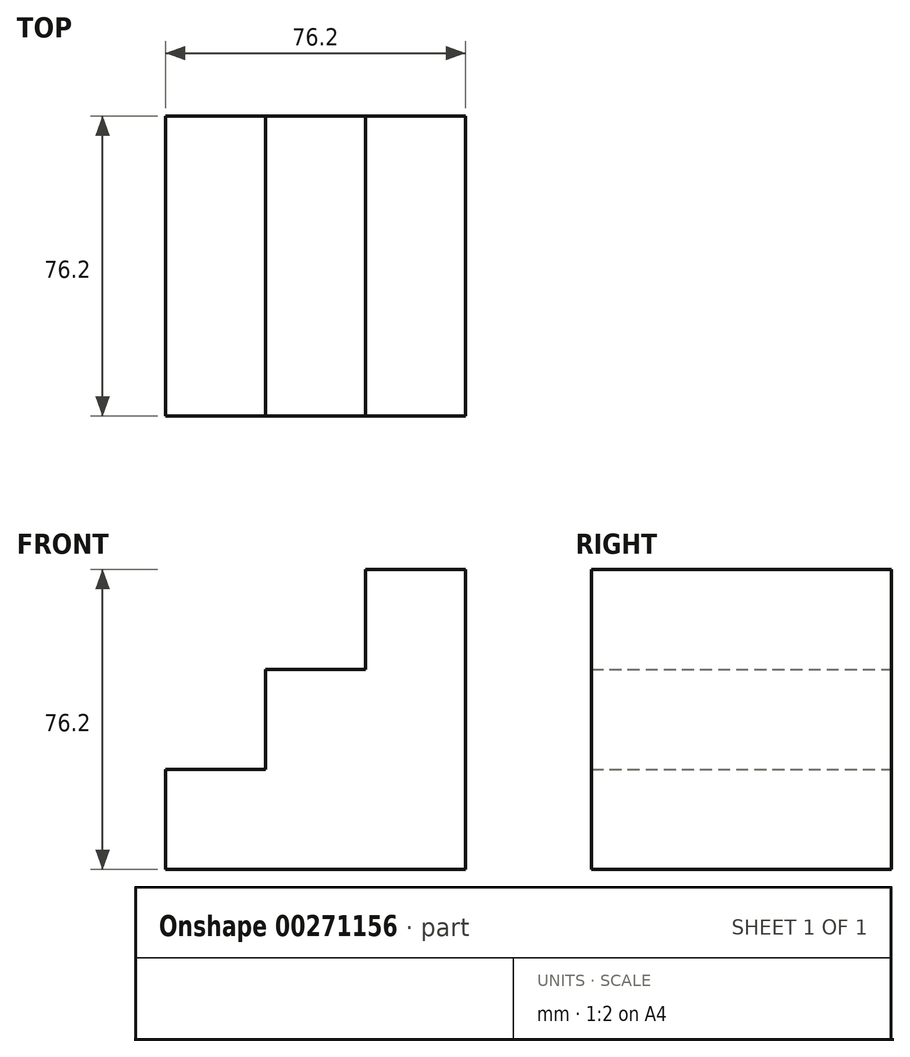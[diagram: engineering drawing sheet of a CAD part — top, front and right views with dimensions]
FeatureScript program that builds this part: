
annotation { "Feature Type Name" : "Feature", "Feature Type Description" : "" }
export const myFeature = defineFeature(function(context is Context, id is Id, definition is map)
    precondition{}
    {
        {
            var Q0;
            Q0=qCreatedBy(makeId("Front.planeOp"),FACE);
            var sketch = newSketch(context, id + "F0", { "sketchPlane" : qUnion([Q0])});
            skLineSegment(sketch, "E0", {"start": v(0, 0) * mm, "end": v(-76.2, 0) * mm});
            skLineSegment(sketch, "E1", {"start": v(-76.2, 0) * mm, "end": v(-76.2, 25.4) * mm});
            skLineSegment(sketch, "E2", {"start": v(-76.2, 25.4) * mm, "end": v(-50.8, 25.4) * mm});
            skLineSegment(sketch, "E3", {"start": v(-50.8, 25.4) * mm, "end": v(-50.8, 50.8) * mm});
            skLineSegment(sketch, "E4", {"start": v(-50.8, 50.8) * mm, "end": v(-25.4, 50.8) * mm});
            skLineSegment(sketch, "E5", {"start": v(-25.4, 50.8) * mm, "end": v(-25.4, 76.2) * mm});
            skLineSegment(sketch, "E6", {"start": v(-25.4, 76.2) * mm, "end": v(0, 76.2) * mm});
            skLineSegment(sketch, "E7", {"start": v(0, 76.2) * mm, "end": v(0, 0) * mm});
            skSolve(sketch);
        }
        {
            var Q0;
            Q0=makeQuery(id+"F0.imprint","IMPRINT",FACE,{"disambiguationData":[TD([[makeQuery(id+"F0.imprint","IMPRINT",EDGE,{"derivedFrom":sQuery(id+"F0.wireOp",EDGE,"E0")}),-1.0]])]});
            extrude(context, id + "F1", {"entities" : qUnion([Q0]), "depth" : 76.2 * mm});
        }
    });
